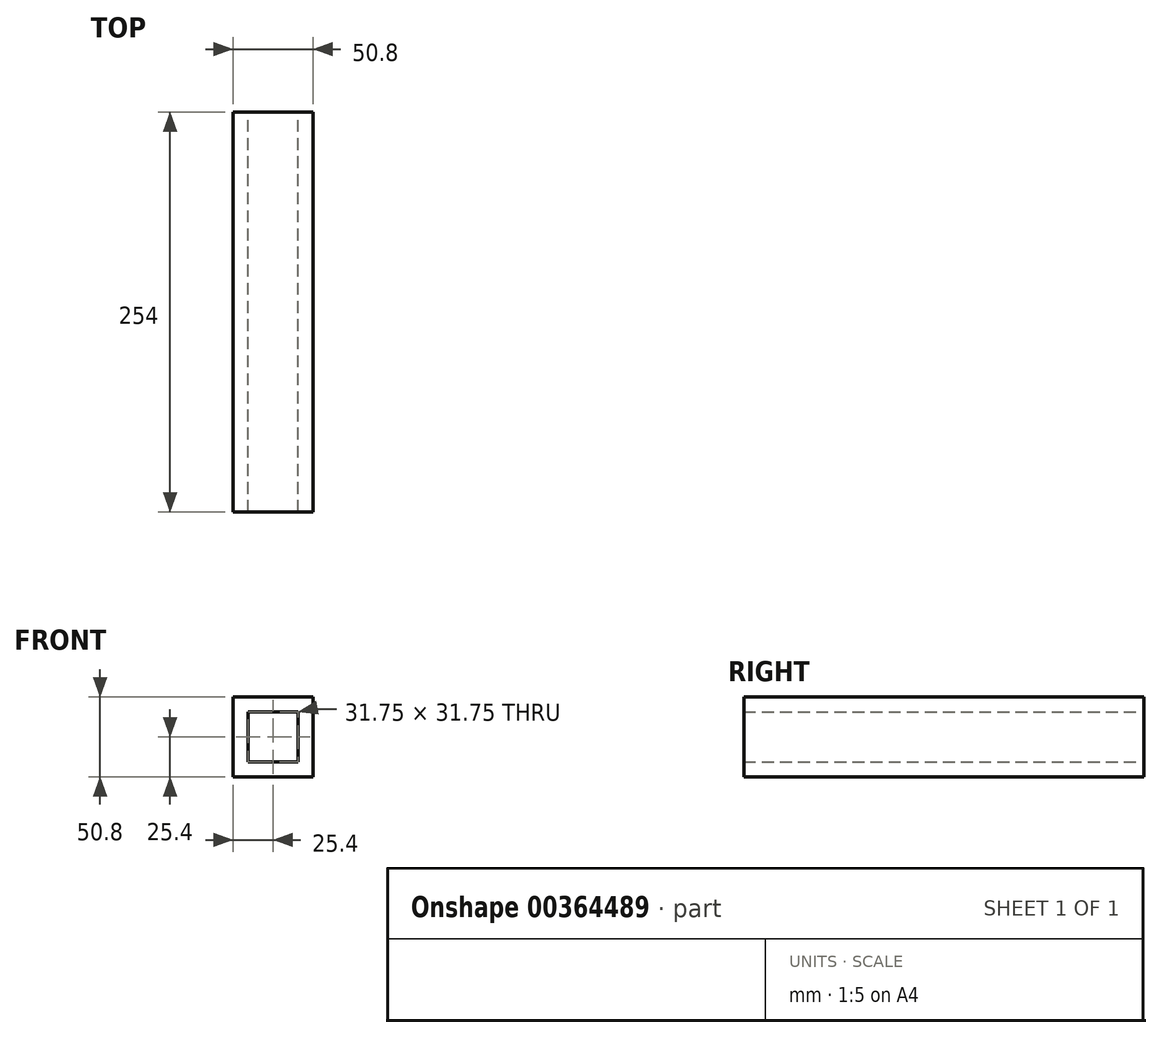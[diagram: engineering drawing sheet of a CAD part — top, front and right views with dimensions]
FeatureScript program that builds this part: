
annotation { "Feature Type Name" : "Feature", "Feature Type Description" : "" }
export const myFeature = defineFeature(function(context is Context, id is Id, definition is map)
    precondition{}
    {
        {
            var Q0;
            Q0=qCreatedBy(makeId("Front.planeOp"),FACE);
            var sketch = newSketch(context, id + "F0", { "sketchPlane" : qUnion([Q0])});
            skLineSegment(sketch, "E0.bottom", {"start": v(0, 0) * mm, "end": v(50.8, 0) * mm});
            skLineSegment(sketch, "E0.top", {"start": v(0, 50.8) * mm, "end": v(50.8, 50.8) * mm});
            skLineSegment(sketch, "E0.left", {"start": v(0, 0) * mm, "end": v(0, 50.8) * mm});
            skLineSegment(sketch, "E0.right", {"start": v(50.8, 0) * mm, "end": v(50.8, 50.8) * mm});
            skLineSegment(sketch, "E1.bottom", {"start": v(9.52, 41.28) * mm, "end": v(41.27, 41.28) * mm});
            skLineSegment(sketch, "E1.top", {"start": v(9.53, 9.53) * mm, "end": v(41.28, 9.53) * mm});
            skLineSegment(sketch, "E1.left", {"start": v(9.52, 41.28) * mm, "end": v(9.53, 9.52) * mm});
            skLineSegment(sketch, "E1.right", {"start": v(41.27, 41.28) * mm, "end": v(41.28, 9.53) * mm});
            skSolve(sketch);
        }
        {
            var Q0;
            Q0=makeQuery(id+"F0.imprint","IMPRINT",FACE,{"disambiguationData":[TD([[makeQuery(id+"F0.imprint","IMPRINT",EDGE,{"derivedFrom":sQuery(id+"F0.wireOp",EDGE,"E0.bottom")}),1.0]])]});
            extrude(context, id + "F1", {"entities" : qUnion([Q0]), "depth" : 254 * mm, "offsetDistance" : 25.4 * mm});
        }
    });
